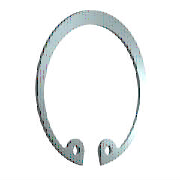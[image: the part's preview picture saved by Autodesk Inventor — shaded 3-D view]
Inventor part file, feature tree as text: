
AUTODESK INVENTOR PART (.ipt)
format: ipt  version: 2023.2 (Build 272271030, 271C)  size: 163,328 bytes
history: native  units: mm (DEFAULTED — no unit token found)
features: sketch x4, plane x3, other x2, hole x2
ambient origin geometry x8: Origin, YZ Plane, XZ Plane, XY Plane, X Axis, Y Axis, Z Axis, Center Point
bodies: Solid1 (feature_tree)
feature tree (11):
  plane  "WorkPlane1"
  plane  "Work Plane2"
  plane  "WorkPlane2"
  sketch  "Sketch1"  dims[d0=-2.0mm d1=5.2mm]
  other  "WorkPoint1"
  other  "WorkAxis1"
  hole  "Hole1"  [1 undecoded]
  hole  "Hole2"  [1 undecoded]
  sketch  "Sketch2"  dims[d2=27.65mm d3=0.0mm]
  sketch  "Sketch3"  dims[d4=0.0mm]
  sketch  "Sketch4"  dims[d5=4.227778mm d6=24.927778mm d7=0.283333mm d8=1.233333mm d9=3.12mm d10=6.5mm d11=3.12mm d12=6.5mm d13=1.08mm d14=2.25mm d15=1.08mm d16=2.25mm d17=3.66mm d18=24.2mm d19=3.66mm d20=24.2mm d21=6.283185mm d22=6.283185mm d23=6.283185mm d24=6.283185mm d25=2.0mm d26=0.0mm d27=0.0mm d28=0.0mm d29=2.5mm d30=6.0mm d31=4.0mm d32=2.0mm d33=60.0deg d34=8.0mm d35=20.594885mm d36=2.5mm d37=6.0mm d38=4.0mm d39=2.0mm d40=60.0deg d41=8.0mm d42=20.594885mm d47=0.0mm d48=0.0mm d49=0.0mm d50=0.0mm]
note: 2 required parameter values undecoded (feature->parameter linkage not recoverable at this tier; creation-order binding heuristic only, values carry confidence <= 0.55)
